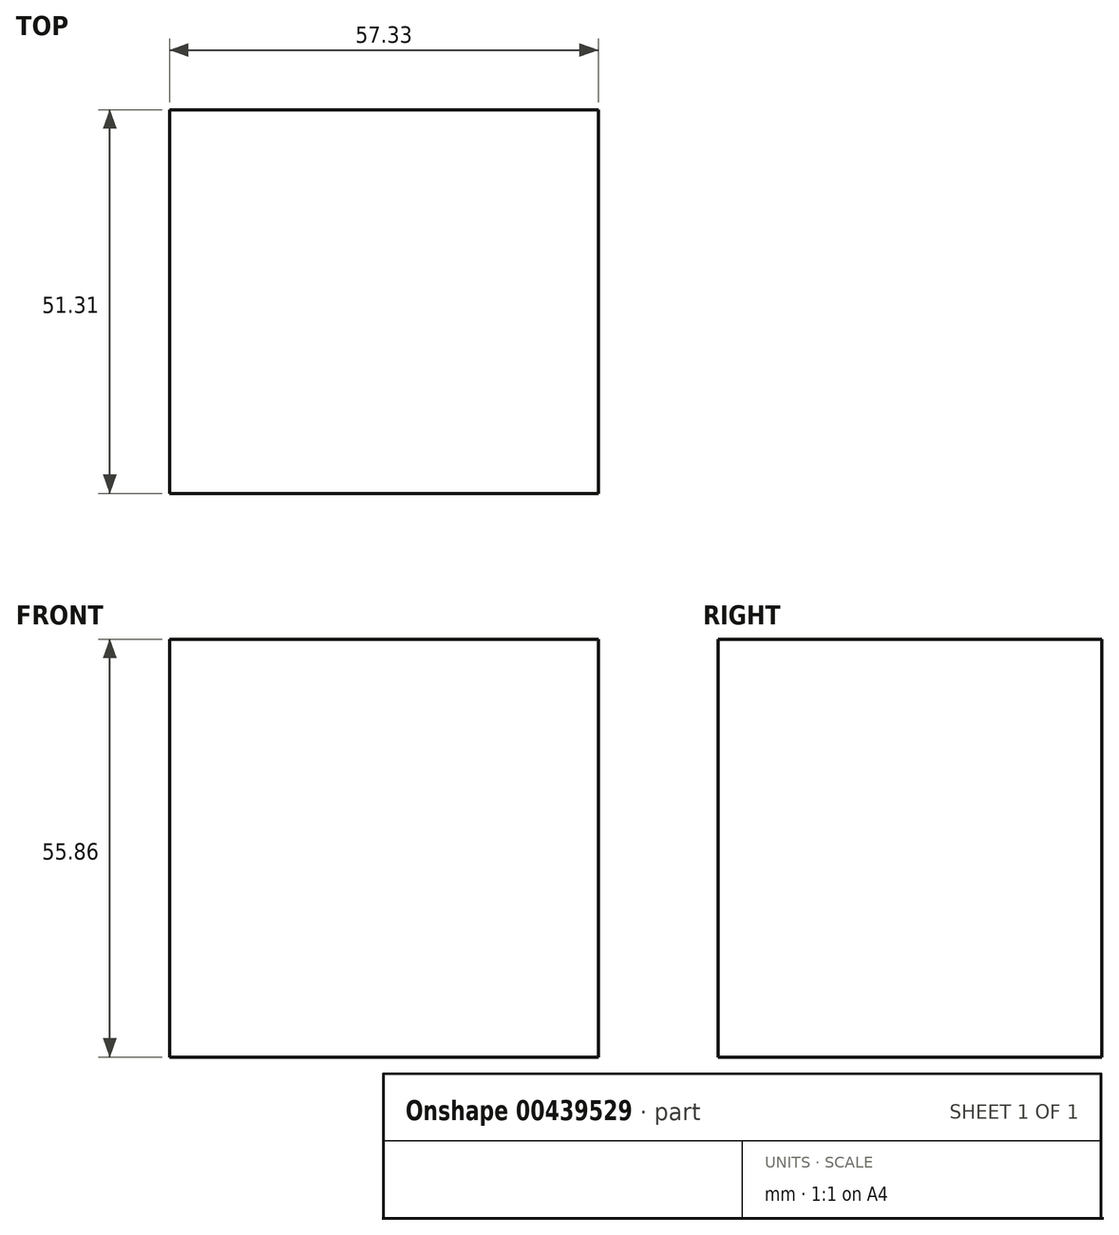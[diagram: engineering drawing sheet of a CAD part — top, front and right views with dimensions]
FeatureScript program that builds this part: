
annotation { "Feature Type Name" : "Feature", "Feature Type Description" : "" }
export const myFeature = defineFeature(function(context is Context, id is Id, definition is map)
    precondition{}
    {
        {
            var Q0;
            Q0=qCreatedBy(makeId("Front.planeOp"),FACE);
            var sketch = newSketch(context, id + "F0", { "sketchPlane" : qUnion([Q0])});
            skLineSegment(sketch, "E0.bottom", {"start": v(0, 55.86) * mm, "end": v(57.33, 55.86) * mm});
            skLineSegment(sketch, "E0.top", {"start": v(0, 0) * mm, "end": v(57.33, 0) * mm});
            skLineSegment(sketch, "E0.left", {"start": v(0, 55.86) * mm, "end": v(0, 0) * mm});
            skLineSegment(sketch, "E0.right", {"start": v(57.33, 55.86) * mm, "end": v(57.33, 0) * mm});
            skSolve(sketch);
        }
        {
            var Q0;
            Q0=makeQuery(id+"F0.imprint","IMPRINT",FACE,{"disambiguationData":[TD([[makeQuery(id+"F0.imprint","IMPRINT",EDGE,{"derivedFrom":sQuery(id+"F0.wireOp",EDGE,"E0.bottom")}),-1.0]])]});
            extrude(context, id + "F1", {"entities" : qUnion([Q0]), "depth" : 51.3 * mm});
        }
    });
